# Revit family: 400 Inset
name_source: partatom
category: Plumbing Fixtures
units: mm (PartAtom-declared; Revit-internal decimal feet)

## family parameters
Cut with Voids When Loaded = Yes
Host = Face
OmniClass Number = 23.45.05.14.14
OmniClass Title = Sinks/Lavatories
Part Type = Normal
Room Calculation Point = No
Round Connector Dimension = Use Diameter
Shared = No

## types (7) — shared parameters
Assembly Code = D2010400
CW Connection = No
HW Connection = No
Manufacturer = GWA Bathrooms & Kitchens
URL = https://www.caroma.com.au
Vent Connection = No
Waste Connection = Yes
zero-valued in all types: Default Elevation

## per-type parameters (varying)
| type | Material_Basin | Material_Waste | Model |
| LIANO II 400 ROUND INSET BASIN NTH NOF WHITE | GWA-Porcelain-White | GWA-Porcelain-White | 852400W |
| LIANO II 400 ROUND INSET BASIN NTH NOF MATTE WHITE | GWA-Porcelain-Matte-White | GWA-Porcelain-Matte-White | 852400MW |
| LIANO II 400 ROUND INSET BASIN NTH NOF MATTE GREEN | GWA-Porcelain-Green | GWA-Porcelain-Green | 852400MG |
| LIANO II 400 ROUND INSET BASIN NTH NOF MATTE BLACK | GWA-Porcelain-Black | GWA-Porcelain-Black | 852400MB |
| LIANO II 400 ROUND INSET BASIN NTH NOF MATTE PINK | GWA-Porcelain-Pink | GWA-Porcelain-Pink | 852400MP |
| LIANO II 400 ROUND INSET BASIN NTH NOF MATTE GREY | GWA-Porcelain-Grey | GWA-Porcelain-Grey | 852400MGR |
| LIANO II 400 ROUND INSET BASIN NTH NOF MATTE SPECKLED | GWA-Porcelain-Speckled | GWA-Porcelain-Speckled | 852400MS |

note: column(s) folded — value = type name in every type: Description

## geometry (parser evidence)
native form markers: Sweep x2
no freeform markers — native parametric forms only
